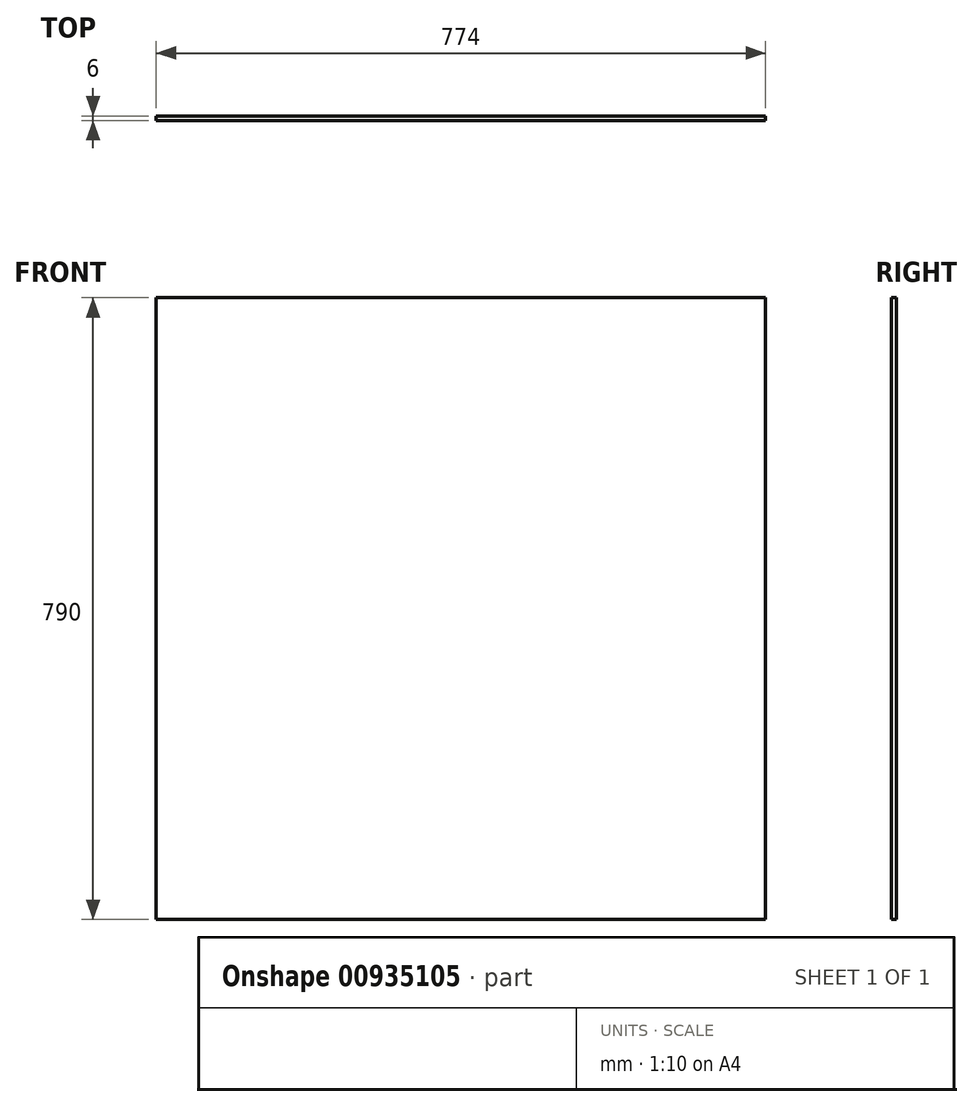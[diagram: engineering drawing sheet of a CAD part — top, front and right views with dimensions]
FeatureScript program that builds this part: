
annotation { "Feature Type Name" : "Feature", "Feature Type Description" : "" }
export const myFeature = defineFeature(function(context is Context, id is Id, definition is map)
    precondition{}
    {
        {
            var Q0;
            Q0=qCreatedBy(makeId("Front.planeOp"),FACE);
            var sketch = newSketch(context, id + "F0", { "sketchPlane" : qUnion([Q0])});
            skLineSegment(sketch, "E0.bottom", {"start": v(0, 0) * mm, "end": v(774, 0) * mm});
            skLineSegment(sketch, "E0.top", {"start": v(0, 790) * mm, "end": v(774, 790) * mm});
            skLineSegment(sketch, "E0.left", {"start": v(0, 0) * mm, "end": v(0, 790) * mm});
            skLineSegment(sketch, "E0.right", {"start": v(774, 0) * mm, "end": v(774, 790) * mm});
            skSolve(sketch);
        }
        {
            var Q0;
            Q0=makeQuery(id+"F0.imprint","IMPRINT",FACE,{"disambiguationData":[TD([[makeQuery(id+"F0.imprint","IMPRINT",EDGE,{"derivedFrom":sQuery(id+"F0.wireOp",EDGE,"E0.bottom")}),1.0]])]});
            extrude(context, id + "F1", {"entities" : qUnion([Q0]), "depth" : 6 * mm, "offsetDistance" : 25 * mm});
        }
    });
